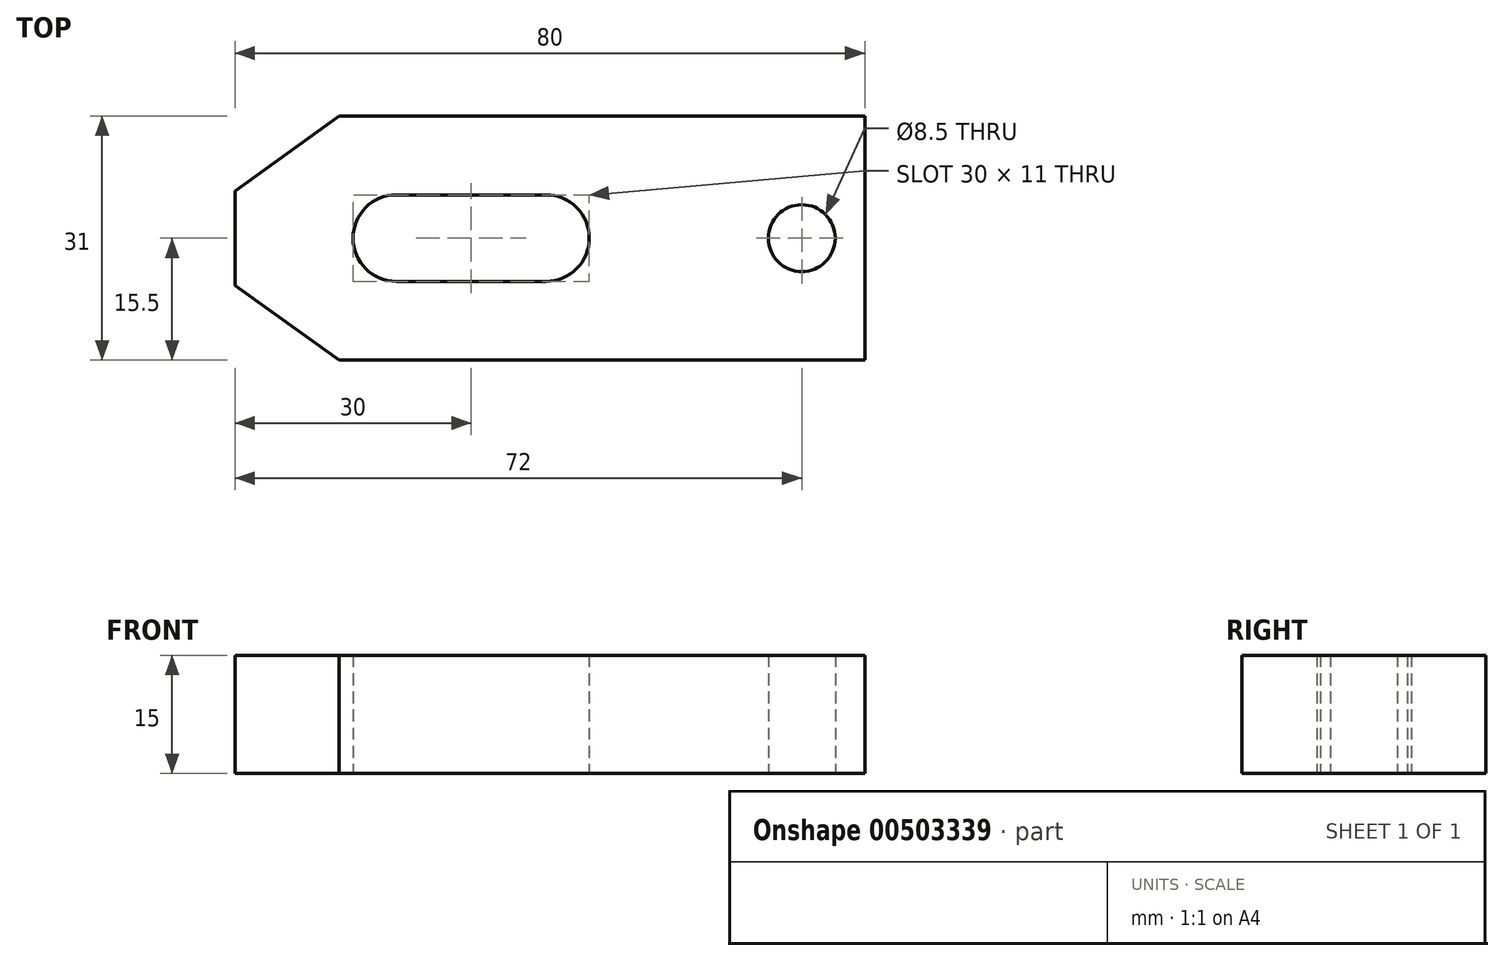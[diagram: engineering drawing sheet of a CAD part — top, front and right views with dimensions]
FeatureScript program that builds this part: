
annotation { "Feature Type Name" : "Feature", "Feature Type Description" : "" }
export const myFeature = defineFeature(function(context is Context, id is Id, definition is map)
    precondition{}
    {
        {
            var Q0;
            Q0=qCreatedBy(makeId("Top.planeOp"),FACE);
            var sketch = newSketch(context, id + "F0", { "sketchPlane" : qUnion([Q0])});
            skLineSegment(sketch, "E0.right", {"start": v(80, 0) * mm, "end": v(80, 31) * mm});
            skLineSegment(sketch, "E1", {"start": v(39.5, 15.5) * mm, "end": v(20.5, 15.5) * mm});
            skPoint(sketch, "E1.startSnap0", {"position": v(80, 15.5) * mm});
            skPoint(sketch, "E1.endSnap0", {"position": v(80, 15.5) * mm});
            skArc(sketch, "E2.0.startCap", {"start": v(39.5, 21) * mm, "mid": v(45, 15.5) * mm, "end": v(39.5, 10) * mm});
            skArc(sketch, "E2.0.endCap", {"start": v(20.5, 10) * mm, "mid": v(15, 15.5) * mm, "end": v(20.5, 21) * mm});
            skLineSegment(sketch, "E2.0.left", {"start": v(39.5, 10) * mm, "end": v(20.5, 10) * mm});
            skLineSegment(sketch, "E2.0.right", {"start": v(39.5, 21) * mm, "end": v(20.5, 21) * mm});
            skLineSegment(sketch, "E3", {"start": v(0, 9.5) * mm, "end": v(0, 21.5) * mm});
            skLineSegment(sketch, "E4", {"start": v(80, 0) * mm, "end": v(13.21, 0) * mm});
            skLineSegment(sketch, "E5", {"start": v(13.21, 0) * mm, "end": v(0, 9.5) * mm});
            skLineSegment(sketch, "E6", {"start": v(80, 31) * mm, "end": v(13.21, 31) * mm});
            skLineSegment(sketch, "E7", {"start": v(13.21, 31) * mm, "end": v(0, 21.5) * mm});
            skCircle(sketch, "E8", {"center": v(72, 15.5) * mm, "radius": 4.25 * mm});
            skSolve(sketch);
        }
        {
            var Q0;
            Q0=makeQuery(id+"F0.imprint","IMPRINT",FACE,{"disambiguationData":[TD([[makeQuery(id+"F0.imprint","IMPRINT",EDGE,{"derivedFrom":sQuery(id+"F0.wireOp",EDGE,"E0.right")}),1.0]])]});
            extrude(context, id + "F1", {"entities" : qUnion([Q0]), "depth" : 15 * mm});
        }
    });
